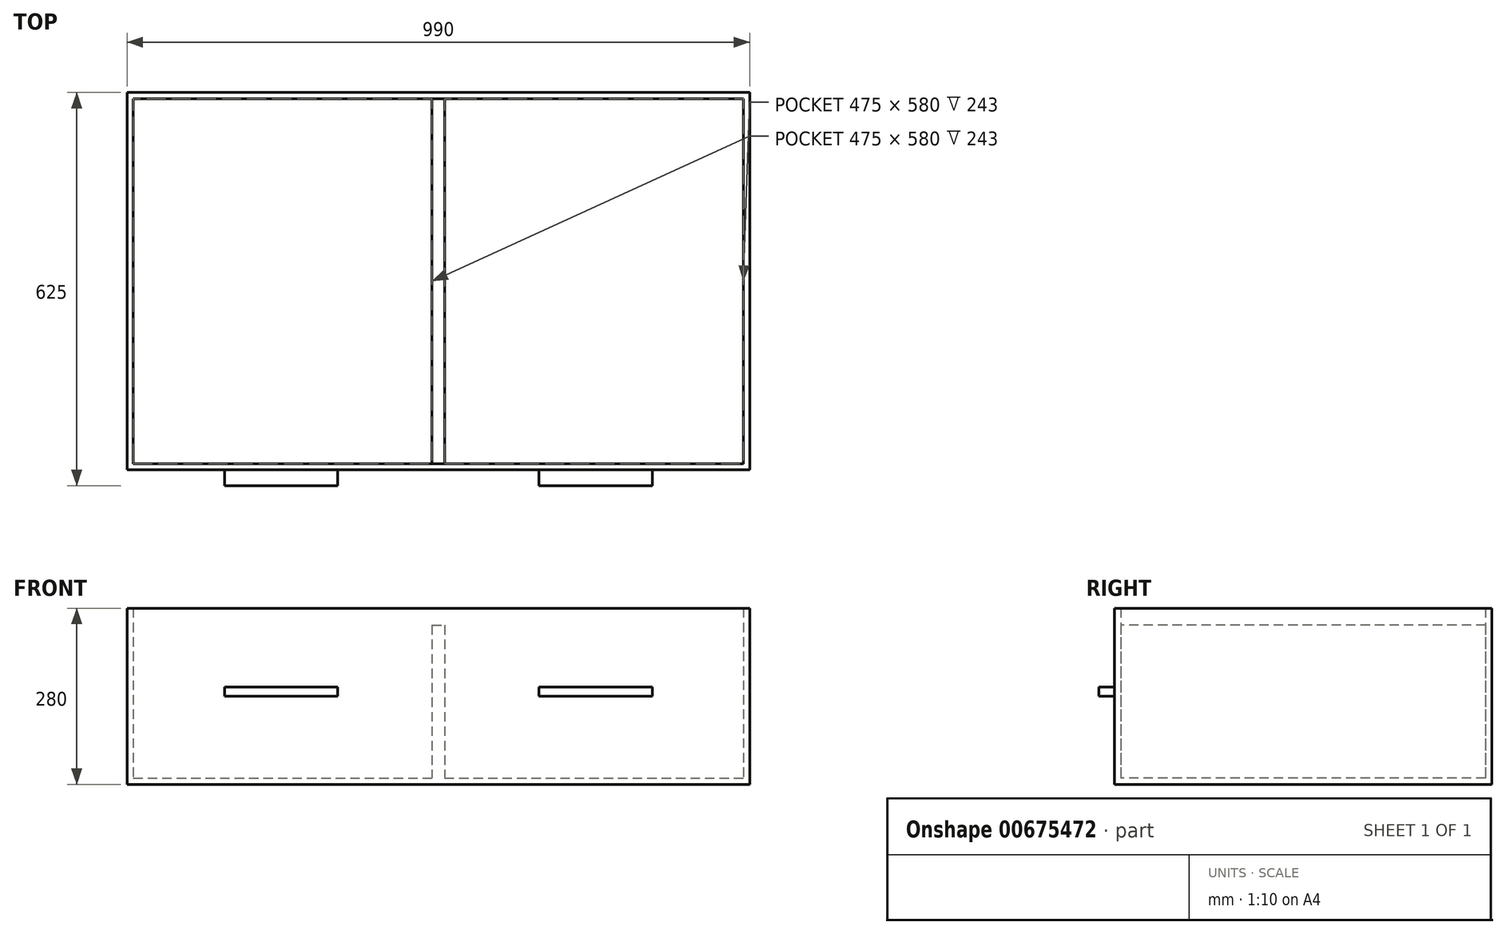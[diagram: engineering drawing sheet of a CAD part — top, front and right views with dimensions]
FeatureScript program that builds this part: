
annotation { "Feature Type Name" : "Feature", "Feature Type Description" : "" }
export const myFeature = defineFeature(function(context is Context, id is Id, definition is map)
    precondition{}
    {
        {
            var Q0;
            Q0=qCreatedBy(makeId("Front.planeOp"),FACE);
            var sketch = newSketch(context, id + "F0", { "sketchPlane" : qUnion([Q0])});
            skLineSegment(sketch, "E0.bottom", {"start": v(-495, 140) * mm, "end": v(495, 140) * mm});
            skLineSegment(sketch, "E0.top", {"start": v(-495, -140) * mm, "end": v(495, -140) * mm});
            skLineSegment(sketch, "E0.left", {"start": v(-495, 140) * mm, "end": v(-495, -140) * mm});
            skLineSegment(sketch, "E0.right", {"start": v(495, 140) * mm, "end": v(495, -140) * mm});
            skPoint(sketch, "E0.middle", {"position": v(0, 0) * mm});
            skSolve(sketch);
        }
        {
            var Q0;
            Q0=makeQuery(id+"F0.imprint","IMPRINT",FACE,{"disambiguationData":[TD([[makeQuery(id+"F0.imprint","IMPRINT",EDGE,{"derivedFrom":sQuery(id+"F0.wireOp",EDGE,"E0.bottom")}),-1.0]])]});
            extrude(context, id + "F1", {"entities" : qUnion([Q0]), "depth" : 600 * mm, "offsetDistance" : 25 * mm});
        }
        {
            var Q0;
            Q0=makeQuery(id+"F1.opExtrude","SWEPT_FACE",FACE,{"disambiguationData":[OSD([sQuery(id+"F0.wireOp",EDGE,"E0.bottom")])]});
            shell(context, id + "F2", {"entities" : qUnion([Q0]), "thickness" : 10 * mm});
        }
        {
            var Q0;
            Q0=makeQuery(id+"F2.opShell","OFFSET_FACE",FACE,{"disambiguationData":[OSD([sQuery(id+"F0.wireOp",EDGE,"E0.top")])]});
            var sketch = newSketch(context, id + "F3", { "sketchPlane" : qUnion([Q0])});
            skLineSegment(sketch, "E1.bottom", {"start": v(-10, -10) * mm, "end": v(10, -10) * mm});
            skLineSegment(sketch, "E1.top", {"start": v(-10, -590) * mm, "end": v(10, -590) * mm});
            skLineSegment(sketch, "E1.left", {"start": v(-10, -10) * mm, "end": v(-10, -590) * mm});
            skLineSegment(sketch, "E1.right", {"start": v(10, -10) * mm, "end": v(10, -590) * mm});
            skSolve(sketch);
        }
        {
            var Q0;
            Q0=makeQuery(id+"F3.imprint","IMPRINT",FACE,{"disambiguationData":[TD([[makeQuery(id+"F3.imprint","IMPRINT",EDGE,{"derivedFrom":sQuery(id+"F3.wireOp",EDGE,"E1.bottom")}),-1.0]])]});
            extrude(context, id + "F4", {"entities" : qUnion([Q0]), "operationType" : NewBodyOperationType.ADD, "depth" : 243 * mm, "offsetDistance" : 25 * mm});
        }
        {
            var Q0;
            Q0=makeQuery(id+"F1.opExtrude","CAP_FACE",FACE,{"disambiguationData":[OSD([sQuery(id+"F0.wireOp",EDGE,"E0.bottom"),sQuery(id+"F0.wireOp",EDGE,"E0.top"),sQuery(id+"F0.wireOp",EDGE,"E0.left"),sQuery(id+"F0.wireOp",EDGE,"E0.right")])],"isStart":false});
            var sketch = newSketch(context, id + "F5", { "sketchPlane" : qUnion([Q0])});
            skLineSegment(sketch, "E2.bottom", {"start": v(-340, 15) * mm, "end": v(-160, 15) * mm});
            skLineSegment(sketch, "E2.top", {"start": v(-340, 0) * mm, "end": v(-160, 0) * mm});
            skLineSegment(sketch, "E2.left", {"start": v(-340, 15) * mm, "end": v(-340, 0) * mm});
            skLineSegment(sketch, "E2.right", {"start": v(-160, 15) * mm, "end": v(-160, 0) * mm});
            skLineSegment(sketch, "E3.bottom", {"start": v(160, 15) * mm, "end": v(340, 15) * mm});
            skLineSegment(sketch, "E3.top", {"start": v(160, 0) * mm, "end": v(340, 0) * mm});
            skLineSegment(sketch, "E3.left", {"start": v(160, 15) * mm, "end": v(160, 0) * mm});
            skLineSegment(sketch, "E3.right", {"start": v(340, 15) * mm, "end": v(340, 0) * mm});
            skSolve(sketch);
        }
        {
            var Q0;
            Q0=makeQuery(id+"F5.imprint","IMPRINT",FACE,{"disambiguationData":[TD([[makeQuery(id+"F5.imprint","IMPRINT",EDGE,{"derivedFrom":sQuery(id+"F5.wireOp",EDGE,"E3.bottom")}),-1.0]])]});
            var Q1;
            Q1=makeQuery(id+"F5.imprint","IMPRINT",FACE,{"disambiguationData":[TD([[makeQuery(id+"F5.imprint","IMPRINT",EDGE,{"derivedFrom":sQuery(id+"F5.wireOp",EDGE,"E2.bottom")}),-1.0]])]});
            extrude(context, id + "F6", {"entities" : qUnion([Q0, Q1]), "operationType" : NewBodyOperationType.ADD, "depth" : 25 * mm, "offsetDistance" : 25 * mm});
        }
    });
